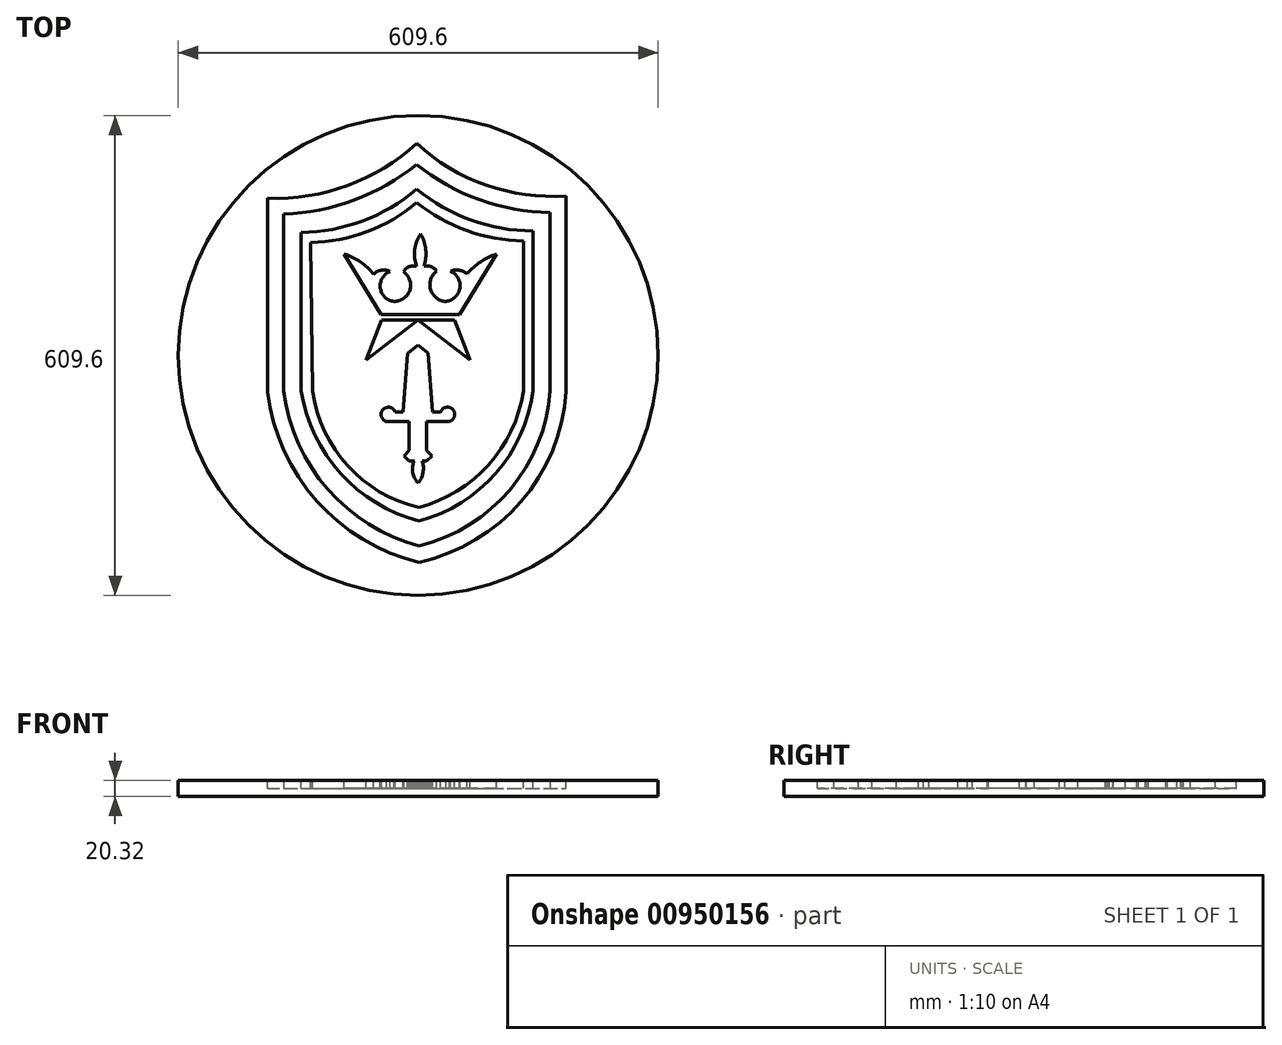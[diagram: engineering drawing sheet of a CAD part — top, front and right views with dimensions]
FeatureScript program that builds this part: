
annotation { "Feature Type Name" : "Feature", "Feature Type Description" : "" }
export const myFeature = defineFeature(function(context is Context, id is Id, definition is map)
    precondition{}
    {
        {
            var Q0;
            Q0=qCreatedBy(makeId("Top.planeOp"),FACE);
            var sketch = newSketch(context, id + "F0", { "sketchPlane" : qUnion([Q0])});
            skPoint(sketch, "E0.0", {"position": v(-45.7, 36.46) * mm});
            skPoint(sketch, "E1.0", {"position": v(53.8, 36.46) * mm});
            skPoint(sketch, "E2.0", {"position": v(100.8, 113.13) * mm});
            skPoint(sketch, "E3.0", {"position": v(63.63, 88.13) * mm});
            skPoint(sketch, "E4.0", {"position": v(42.63, 91.3) * mm});
            skPoint(sketch, "E5.0", {"position": v(25.13, 91.46) * mm});
            skPoint(sketch, "E6.0", {"position": v(8.8, 97.63) * mm});
            skPoint(sketch, "E7.0", {"position": v(-0.37, 97.46) * mm});
            skPoint(sketch, "E8.0", {"position": v(-17.03, 90.63) * mm});
            skPoint(sketch, "E9.0", {"position": v(-34.03, 91.13) * mm});
            skPoint(sketch, "E10.0", {"position": v(-55.2, 87.63) * mm});
            skPoint(sketch, "E11.0", {"position": v(-92.37, 113.13) * mm});
            skPoint(sketch, "E12.0", {"position": v(-64.53, -21.7) * mm});
            skPoint(sketch, "E13.0", {"position": v(-44.87, 29.46) * mm});
            skPoint(sketch, "E14.0", {"position": v(1.47, 29.46) * mm});
            skPoint(sketch, "E15.0", {"position": v(67.47, -21.7) * mm});
            skPoint(sketch, "E16.0", {"position": v(47.8, 29.46) * mm});
            skPoint(sketch, "E17.0", {"position": v(1.25, -2.29) * mm});
            skPoint(sketch, "E18.0", {"position": v(-12.12, -13.12) * mm});
            skPoint(sketch, "E19.0", {"position": v(-17.53, -87.54) * mm});
            skPoint(sketch, "E20.0", {"position": v(-27.71, -87.46) * mm});
            skPoint(sketch, "E21.0", {"position": v(-38.85, -99.54) * mm});
            skPoint(sketch, "E22.0", {"position": v(-10, -99.54) * mm});
            skPoint(sketch, "E23.0", {"position": v(12.13, -99.54) * mm});
            skPoint(sketch, "E24.0", {"position": v(29.97, -87.48) * mm});
            skPoint(sketch, "E25.0", {"position": v(19.97, -87.54) * mm});
            skPoint(sketch, "E26.0", {"position": v(14.13, -12.7) * mm});
            skPoint(sketch, "E27.0", {"position": v(19.02, -143.57) * mm});
            skPoint(sketch, "E28.0", {"position": v(12.3, -136.2) * mm});
            skPoint(sketch, "E29.0", {"position": v(-10.23, -136.2) * mm});
            skPoint(sketch, "E30.0", {"position": v(-16.22, -143.37) * mm});
            skPoint(sketch, "E31.0", {"position": v(-10.2, -149.54) * mm});
            skPoint(sketch, "E32.0", {"position": v(-3.2, -149.54) * mm});
            skPoint(sketch, "E33.0", {"position": v(1.8, -177.7) * mm});
            skPoint(sketch, "E34.0", {"position": v(6.61, -149.6) * mm});
            skPoint(sketch, "E35.0", {"position": v(11.99, -149.48) * mm});
            skPoint(sketch, "E36.0", {"position": v(-135.23, 127.8) * mm});
            skPoint(sketch, "E37.0", {"position": v(-147.23, 140.49) * mm});
            skPoint(sketch, "E38.0", {"position": v(-169.23, 163.75) * mm});
            skPoint(sketch, "E39.0", {"position": v(-0.37, 195.5) * mm});
            skPoint(sketch, "E40.0", {"position": v(-0.34, 178.32) * mm});
            skPoint(sketch, "E41.0", {"position": v(135.23, 129.67) * mm});
            skPoint(sketch, "E42.0", {"position": v(169.23, 166.1) * mm});
            skPoint(sketch, "E43.0", {"position": v(-0.43, 226.98) * mm});
            skPoint(sketch, "E44.0", {"position": v(2.93, -257.46) * mm});
            skPoint(sketch, "E45.0", {"position": v(2.55, -225.97) * mm});
            skPoint(sketch, "E46.0", {"position": v(2.34, -208.8) * mm});
            skLineSegment(sketch, "E47", {"start": v(-64.53, -21.7) * mm, "end": v(1.47, 29.46) * mm});
            skLineSegment(sketch, "E48", {"start": v(-44.87, 29.46) * mm, "end": v(-64.53, -21.7) * mm});
            skLineSegment(sketch, "E49", {"start": v(-44.87, 29.46) * mm, "end": v(1.47, 29.46) * mm});
            skLineSegment(sketch, "E50", {"start": v(1.47, 29.46) * mm, "end": v(47.8, 29.46) * mm});
            skLineSegment(sketch, "E51", {"start": v(67.47, -21.7) * mm, "end": v(47.8, 29.46) * mm});
            skLineSegment(sketch, "E52", {"start": v(67.47, -21.7) * mm, "end": v(1.47, 29.46) * mm});
            skLineSegment(sketch, "E53", {"start": v(1.25, -2.29) * mm, "end": v(-12.12, -13.12) * mm});
            skLineSegment(sketch, "E54", {"start": v(1.25, -2.29) * mm, "end": v(14.13, -12.7) * mm});
            skLineSegment(sketch, "E55", {"start": v(-12.12, -13.12) * mm, "end": v(-17.53, -87.54) * mm});
            skLineSegment(sketch, "E56", {"start": v(-17.53, -87.54) * mm, "end": v(-27.71, -87.46) * mm});
            skLineSegment(sketch, "E57", {"start": v(19.97, -87.54) * mm, "end": v(29.97, -87.48) * mm});
            skPoint(sketch, "E58.0", {"position": v(41.07, -99.54) * mm});
            skLineSegment(sketch, "E59", {"start": v(-38.85, -99.54) * mm, "end": v(-10, -99.54) * mm});
            skLineSegment(sketch, "E60", {"start": v(12.13, -99.54) * mm, "end": v(41.07, -99.54) * mm});
            skLineSegment(sketch, "E61", {"start": v(-10.23, -136.2) * mm, "end": v(-10, -99.54) * mm});
            skLineSegment(sketch, "E62", {"start": v(12.13, -99.54) * mm, "end": v(12.3, -136.2) * mm});
            skLineSegment(sketch, "E63", {"start": v(-10.23, -136.2) * mm, "end": v(-16.22, -143.37) * mm});
            skLineSegment(sketch, "E64", {"start": v(-16.22, -143.37) * mm, "end": v(-10.2, -149.54) * mm});
            skLineSegment(sketch, "E65", {"start": v(-10.2, -149.54) * mm, "end": v(-3.2, -149.54) * mm});
            skLineSegment(sketch, "E66", {"start": v(6.61, -149.6) * mm, "end": v(11.99, -149.48) * mm});
            skLineSegment(sketch, "E67", {"start": v(11.99, -149.48) * mm, "end": v(19.02, -143.57) * mm});
            skLineSegment(sketch, "E68", {"start": v(19.02, -143.57) * mm, "end": v(12.3, -136.2) * mm});
            skArc(sketch, "E69", {"start": v(-34.03, 91.13) * mm, "mid": v(-45.15, 92.6) * mm, "end": v(-55.2, 87.63) * mm});
            skArc(sketch, "E70", {"start": v(-55.2, 87.63) * mm, "mid": v(-71.81, 103.25) * mm, "end": v(-92.37, 113.13) * mm});
            skArc(sketch, "E71", {"start": v(-0.37, 97.46) * mm, "mid": v(-9.95, 97.09) * mm, "end": v(-17.03, 90.63) * mm});
            skArc(sketch, "E72", {"start": v(25.13, 91.46) * mm, "mid": v(17.9, 97) * mm, "end": v(8.8, 97.63) * mm});
            skPoint(sketch, "E73.0", {"position": v(4.8, 138.8) * mm});
            skArc(sketch, "E74", {"start": v(4.8, 138.8) * mm, "mid": v(-2.9, 118.77) * mm, "end": v(-0.37, 97.46) * mm});
            skArc(sketch, "E75", {"start": v(8.8, 97.63) * mm, "mid": v(11.16, 118.63) * mm, "end": v(4.8, 138.8) * mm});
            skArc(sketch, "E76", {"start": v(-34.03, 91.13) * mm, "mid": v(-46.67, 70.15) * mm, "end": v(-29.22, 52.98) * mm});
            skArc(sketch, "E77", {"start": v(-29.22, 52.98) * mm, "mid": v(-9.14, 67.28) * mm, "end": v(-17.03, 90.63) * mm});
            skArc(sketch, "E78", {"start": v(25.13, 91.46) * mm, "mid": v(17.18, 68.05) * mm, "end": v(36.78, 52.98) * mm});
            skArc(sketch, "E79", {"start": v(36.78, 52.98) * mm, "mid": v(54.45, 69.88) * mm, "end": v(42.63, 91.3) * mm});
            skArc(sketch, "E80", {"start": v(63.63, 88.13) * mm, "mid": v(53.57, 92.64) * mm, "end": v(42.63, 91.3) * mm});
            skArc(sketch, "E81", {"start": v(100.8, 113.13) * mm, "mid": v(80.58, 103.06) * mm, "end": v(63.63, 88.13) * mm});
            skLineSegment(sketch, "E82", {"start": v(53.8, 36.46) * mm, "end": v(100.8, 113.13) * mm});
            skLineSegment(sketch, "E83", {"start": v(-45.7, 36.46) * mm, "end": v(53.8, 36.46) * mm});
            skLineSegment(sketch, "E84", {"start": v(-45.7, 36.46) * mm, "end": v(-92.37, 113.13) * mm});
            skArc(sketch, "E85", {"start": v(-27.71, -87.46) * mm, "mid": v(-43.15, -84.4) * mm, "end": v(-38.85, -99.54) * mm});
            skArc(sketch, "E86", {"start": v(41.07, -99.54) * mm, "mid": v(45.52, -84.3) * mm, "end": v(29.97, -87.48) * mm});
            skArc(sketch, "E87", {"start": v(-3.2, -149.54) * mm, "mid": v(-5.54, -164.48) * mm, "end": v(1.8, -177.7) * mm});
            skArc(sketch, "E88", {"start": v(1.8, -177.7) * mm, "mid": v(7.65, -164.24) * mm, "end": v(6.61, -149.6) * mm});
            skPoint(sketch, "E89.0", {"position": v(135.23, -60.82) * mm});
            skLineSegment(sketch, "E90", {"start": v(135.23, -60.82) * mm, "end": v(-222.02, -60.82) * mm, "construction": true});
            skLineSegment(sketch, "E91", {"start": v(-222.02, -60.82) * mm, "end": v(135.23, -60.82) * mm, "construction": true});
            skLineSegment(sketch, "E92", {"start": v(218.08, -60.82) * mm, "end": v(135.23, -60.82) * mm, "construction": true});
            skLineSegment(sketch, "E93", {"start": v(-135.23, 127.8) * mm, "end": v(-132.62, -60.82) * mm});
            skLineSegment(sketch, "E94", {"start": v(-147.23, 140.49) * mm, "end": v(-147.23, -60.82) * mm});
            skLineSegment(sketch, "E95", {"start": v(135.23, 129.67) * mm, "end": v(135.23, -60.82) * mm});
            skPoint(sketch, "E96.0", {"position": v(147.23, 142.53) * mm});
            skLineSegment(sketch, "E97", {"start": v(147.23, 142.53) * mm, "end": v(147.23, -60.82) * mm});
            skArc(sketch, "E98", {"start": v(-147.23, -60.82) * mm, "mid": v(-96.87, -165.64) * mm, "end": v(2.55, -225.97) * mm});
            skArc(sketch, "E99", {"start": v(2.55, -225.97) * mm, "mid": v(100.07, -165.45) * mm, "end": v(147.23, -60.82) * mm});
            skArc(sketch, "E100", {"start": v(2.34, -208.8) * mm, "mid": v(90.9, -154.67) * mm, "end": v(135.23, -60.82) * mm});
            skArc(sketch, "E101", {"start": v(-132.62, -60.82) * mm, "mid": v(-88.12, -155.77) * mm, "end": v(2.34, -208.8) * mm});
            skArc(sketch, "E102", {"start": v(-0.34, 178.32) * mm, "mid": v(63.44, 142.85) * mm, "end": v(135.23, 129.67) * mm});
            skArc(sketch, "E103", {"start": v(-135.23, 127.8) * mm, "mid": v(-63.43, 141.43) * mm, "end": v(-0.34, 178.32) * mm});
            skArc(sketch, "E104", {"start": v(-147.23, 140.49) * mm, "mid": v(-69.02, 155.21) * mm, "end": v(-0.37, 195.5) * mm});
            skArc(sketch, "E105", {"start": v(-0.37, 195.5) * mm, "mid": v(68.84, 156.23) * mm, "end": v(147.23, 142.53) * mm});
            skArc(sketch, "E106", {"start": v(-0.43, 226.98) * mm, "mid": v(79.25, 182.2) * mm, "end": v(169.23, 166.1) * mm});
            skArc(sketch, "E107", {"start": v(-169.23, 163.75) * mm, "mid": v(-79.71, 181.7) * mm, "end": v(-0.43, 226.98) * mm});
            skLineSegment(sketch, "E108", {"start": v(-169.23, 163.75) * mm, "end": v(-169.23, -60.82) * mm});
            skLineSegment(sketch, "E109", {"start": v(169.23, 166.1) * mm, "end": v(169.23, -60.82) * mm});
            skArc(sketch, "E110", {"start": v(-169.23, -60.82) * mm, "mid": v(-113.37, -185.6) * mm, "end": v(2.93, -257.46) * mm});
            skArc(sketch, "E111", {"start": v(2.93, -257.46) * mm, "mid": v(118.16, -186.27) * mm, "end": v(169.23, -60.82) * mm});
            skSolve(sketch);
        }
        {
            var Q0;
            Q0=qCreatedBy(makeId("Top.planeOp"),FACE);
            var sketch = newSketch(context, id + "F1", { "sketchPlane" : qUnion([Q0])});
            skLineSegment(sketch, "E112.0", {"start": v(-169.23, 163.75) * mm, "end": v(-169.23, -60.82) * mm});
            skArc(sketch, "E113.0", {"start": v(-169.23, -60.82) * mm, "mid": v(-113.37, -185.6) * mm, "end": v(2.93, -257.46) * mm});
            skArc(sketch, "E114.0", {"start": v(2.93, -257.46) * mm, "mid": v(118.16, -186.27) * mm, "end": v(169.23, -60.82) * mm});
            skLineSegment(sketch, "E115.0", {"start": v(169.23, 166.1) * mm, "end": v(169.23, -60.82) * mm});
            skArc(sketch, "E116.0", {"start": v(-0.43, 226.98) * mm, "mid": v(79.25, 182.2) * mm, "end": v(169.23, 166.1) * mm});
            skArc(sketch, "E117.0", {"start": v(-169.23, 163.75) * mm, "mid": v(-79.71, 181.7) * mm, "end": v(-0.43, 226.98) * mm});
            skSolve(sketch);
        }
        {
            var Q0;
            Q0 = qSketchRegion(id + "F1", true);
            extrude(context, id + "F2", {"entities" : qUnion([Q0]), "depth" : 31.75 * mm, "offsetDistance" : 25.4 * mm});
        }
        {
            var Q0;
            Q0=makeQuery(id+"F2.opExtrude","CAP_FACE",FACE,{"disambiguationData":[OSD([sQuery(id+"F1.wireOp",EDGE,"E112.0"),sQuery(id+"F1.wireOp",EDGE,"E113.0"),sQuery(id+"F1.wireOp",EDGE,"E114.0"),sQuery(id+"F1.wireOp",EDGE,"E115.0"),sQuery(id+"F1.wireOp",EDGE,"E116.0"),sQuery(id+"F1.wireOp",EDGE,"E117.0")])],"isStart":false});
            var sketch = newSketch(context, id + "F3", { "sketchPlane" : qUnion([Q0])});
            skLineSegment(sketch, "E118.0", {"start": v(-135.23, 127.8) * mm, "end": v(-132.62, -60.82) * mm});
            skLineSegment(sketch, "E119.0", {"start": v(-147.23, 140.49) * mm, "end": v(-147.23, -60.82) * mm});
            skArc(sketch, "E120.0", {"start": v(-135.23, 127.8) * mm, "mid": v(-63.43, 141.43) * mm, "end": v(-0.34, 178.32) * mm});
            skArc(sketch, "E121.0", {"start": v(-147.23, 140.49) * mm, "mid": v(-69.02, 155.21) * mm, "end": v(-0.37, 195.5) * mm});
            skArc(sketch, "E122.0", {"start": v(-0.34, 178.32) * mm, "mid": v(63.44, 142.85) * mm, "end": v(135.23, 129.67) * mm});
            skArc(sketch, "E123.0", {"start": v(-132.62, -60.82) * mm, "mid": v(-88.12, -155.77) * mm, "end": v(2.34, -208.8) * mm});
            skArc(sketch, "E124.0", {"start": v(-147.23, -60.82) * mm, "mid": v(-96.87, -165.64) * mm, "end": v(2.55, -225.97) * mm});
            skArc(sketch, "E125.0", {"start": v(2.34, -208.8) * mm, "mid": v(90.9, -154.67) * mm, "end": v(135.23, -60.82) * mm});
            skArc(sketch, "E126.0", {"start": v(2.55, -225.97) * mm, "mid": v(100.07, -165.45) * mm, "end": v(147.23, -60.82) * mm});
            skLineSegment(sketch, "E127.0", {"start": v(147.23, 142.53) * mm, "end": v(147.23, -60.82) * mm});
            skLineSegment(sketch, "E128.0", {"start": v(135.23, 129.67) * mm, "end": v(135.23, -60.82) * mm});
            skArc(sketch, "E129.0", {"start": v(-0.37, 195.5) * mm, "mid": v(68.84, 156.23) * mm, "end": v(147.23, 142.53) * mm});
            skSolve(sketch);
        }
        {
            var Q0;
            Q0 = qSketchRegion(id + "F3", true);
            extrude(context, id + "F4", {"entities" : qUnion([Q0]), "operationType" : NewBodyOperationType.REMOVE, "oppositeDirection" : true, "depth" : 11.43 * mm, "offsetDistance" : 25.4 * mm});
        }
        {
            var Q0;
            Q0=makeQuery(id+"F4.boolean.opBoolean","SPLIT",FACE,{"disambiguationData":[TD([makeQuery(id+"F4.opExtrude","SWEPT_FACE",FACE,{"disambiguationData":[OSD([sQuery(id+"F3.wireOp",EDGE,"E118.0")])]})])],"derivedFrom":makeQuery(id+"F2.opExtrude","CAP_FACE",FACE,{"disambiguationData":[OSD([sQuery(id+"F1.wireOp",EDGE,"E112.0"),sQuery(id+"F1.wireOp",EDGE,"E113.0"),sQuery(id+"F1.wireOp",EDGE,"E114.0"),sQuery(id+"F1.wireOp",EDGE,"E115.0"),sQuery(id+"F1.wireOp",EDGE,"E116.0"),sQuery(id+"F1.wireOp",EDGE,"E117.0")])],"isStart":false})});
            var sketch = newSketch(context, id + "F5", { "sketchPlane" : qUnion([Q0])});
            skLineSegment(sketch, "E130.0", {"start": v(-45.7, 36.46) * mm, "end": v(-92.37, 113.13) * mm});
            skArc(sketch, "E131.0", {"start": v(-55.2, 87.63) * mm, "mid": v(-71.81, 103.25) * mm, "end": v(-92.37, 113.13) * mm});
            skArc(sketch, "E132.0", {"start": v(-34.03, 91.13) * mm, "mid": v(-45.15, 92.6) * mm, "end": v(-55.2, 87.63) * mm});
            skArc(sketch, "E133.0", {"start": v(-34.03, 91.13) * mm, "mid": v(-46.67, 70.15) * mm, "end": v(-29.22, 52.98) * mm});
            skArc(sketch, "E134.0", {"start": v(-29.22, 52.98) * mm, "mid": v(-9.14, 67.28) * mm, "end": v(-17.03, 90.63) * mm});
            skPoint(sketch, "E135.0", {"position": v(-17.03, 90.63) * mm});
            skArc(sketch, "E136.0", {"start": v(-0.37, 97.46) * mm, "mid": v(-9.95, 97.09) * mm, "end": v(-17.03, 90.63) * mm});
            skArc(sketch, "E137.0", {"start": v(4.8, 138.8) * mm, "mid": v(-2.9, 118.77) * mm, "end": v(-0.37, 97.46) * mm});
            skArc(sketch, "E138.0", {"start": v(8.8, 97.63) * mm, "mid": v(11.16, 118.63) * mm, "end": v(4.8, 138.8) * mm});
            skArc(sketch, "E139.0", {"start": v(25.13, 91.46) * mm, "mid": v(17.9, 97) * mm, "end": v(8.8, 97.63) * mm});
            skArc(sketch, "E140.0", {"start": v(25.13, 91.46) * mm, "mid": v(17.18, 68.05) * mm, "end": v(36.78, 52.98) * mm});
            skArc(sketch, "E141.0", {"start": v(36.78, 52.98) * mm, "mid": v(54.45, 69.88) * mm, "end": v(42.63, 91.3) * mm});
            skArc(sketch, "E142.0", {"start": v(63.63, 88.13) * mm, "mid": v(53.57, 92.64) * mm, "end": v(42.63, 91.3) * mm});
            skArc(sketch, "E143.0", {"start": v(100.8, 113.13) * mm, "mid": v(80.58, 103.06) * mm, "end": v(63.63, 88.13) * mm});
            skPoint(sketch, "E144.0", {"position": v(77.3, 74.8) * mm});
            skLineSegment(sketch, "E145.0", {"start": v(53.8, 36.46) * mm, "end": v(100.8, 113.13) * mm});
            skLineSegment(sketch, "E146.0", {"start": v(-45.7, 36.46) * mm, "end": v(53.8, 36.46) * mm});
            skLineSegment(sketch, "E147.0", {"start": v(1.47, 29.46) * mm, "end": v(47.8, 29.46) * mm});
            skLineSegment(sketch, "E148.0", {"start": v(67.47, -21.7) * mm, "end": v(1.47, 29.46) * mm});
            skLineSegment(sketch, "E149.0", {"start": v(67.47, -21.7) * mm, "end": v(47.8, 29.46) * mm});
            skLineSegment(sketch, "E150.0", {"start": v(-64.53, -21.7) * mm, "end": v(1.47, 29.46) * mm});
            skPoint(sketch, "E151.0", {"position": v(-21.7, 29.46) * mm});
            skLineSegment(sketch, "E152.0", {"start": v(-44.87, 29.46) * mm, "end": v(1.47, 29.46) * mm});
            skLineSegment(sketch, "E153.0", {"start": v(-44.87, 29.46) * mm, "end": v(-64.53, -21.7) * mm});
            skLineSegment(sketch, "E154.0", {"start": v(-12.12, -13.12) * mm, "end": v(-17.53, -87.54) * mm});
            skLineSegment(sketch, "E155.0", {"start": v(1.25, -2.29) * mm, "end": v(-12.12, -13.12) * mm});
            skPoint(sketch, "E156.0", {"position": v(14.13, -12.7) * mm});
            skPoint(sketch, "E157.0", {"position": v(7.69, -7.5) * mm});
            skPoint(sketch, "E158.0", {"position": v(-22.62, -87.5) * mm});
            skLineSegment(sketch, "E159.0", {"start": v(-17.53, -87.54) * mm, "end": v(-27.71, -87.46) * mm});
            skArc(sketch, "E160.0", {"start": v(-27.71, -87.46) * mm, "mid": v(-43.15, -84.4) * mm, "end": v(-38.85, -99.54) * mm});
            skLineSegment(sketch, "E161.0", {"start": v(-38.85, -99.54) * mm, "end": v(-10, -99.54) * mm});
            skLineSegment(sketch, "E162.0", {"start": v(-10.23, -136.2) * mm, "end": v(-10, -99.54) * mm});
            skLineSegment(sketch, "E163.0", {"start": v(12.13, -99.54) * mm, "end": v(41.07, -99.54) * mm});
            skLineSegment(sketch, "E164.0", {"start": v(19.97, -87.54) * mm, "end": v(29.97, -87.48) * mm});
            skArc(sketch, "E165.0", {"start": v(41.07, -99.54) * mm, "mid": v(45.52, -84.3) * mm, "end": v(29.97, -87.48) * mm});
            skLineSegment(sketch, "E166.0", {"start": v(12.13, -99.54) * mm, "end": v(12.3, -136.2) * mm});
            skLineSegment(sketch, "E167.0", {"start": v(19.02, -143.57) * mm, "end": v(12.3, -136.2) * mm});
            skLineSegment(sketch, "E168.0", {"start": v(-10.23, -136.2) * mm, "end": v(-16.22, -143.37) * mm});
            skLineSegment(sketch, "E169.0", {"start": v(-16.22, -143.37) * mm, "end": v(-10.2, -149.54) * mm});
            skPoint(sketch, "E170.0", {"position": v(-6.7, -149.54) * mm});
            skLineSegment(sketch, "E171.0", {"start": v(-10.2, -149.54) * mm, "end": v(-3.2, -149.54) * mm});
            skArc(sketch, "E172.0", {"start": v(-3.2, -149.54) * mm, "mid": v(-5.54, -164.48) * mm, "end": v(1.8, -177.7) * mm});
            skArc(sketch, "E173.0", {"start": v(1.8, -177.7) * mm, "mid": v(7.65, -164.24) * mm, "end": v(6.61, -149.6) * mm});
            skLineSegment(sketch, "E174.0", {"start": v(6.61, -149.6) * mm, "end": v(11.99, -149.48) * mm});
            skLineSegment(sketch, "E175.0", {"start": v(11.99, -149.48) * mm, "end": v(19.02, -143.57) * mm});
            skLineSegment(sketch, "E176.0", {"start": v(1.25, -2.29) * mm, "end": v(14.13, -12.7) * mm});
            skLineSegment(sketch, "E177", {"start": v(14.13, -12.7) * mm, "end": v(19.97, -87.54) * mm});
            skSolve(sketch);
        }
        {
            var Q0;
            Q0=makeQuery(id+"F5.imprint","IMPRINT",FACE,{"disambiguationData":[TD([[makeQuery(id+"F5.imprint","IMPRINT",EDGE,{"derivedFrom":sQuery(id+"F5.wireOp",EDGE,"E130.0")}),-1.0]])]});
            extrude(context, id + "F6", {"entities" : qUnion([Q0]), "operationType" : NewBodyOperationType.REMOVE, "oppositeDirection" : true, "depth" : 8.9 * mm, "offsetDistance" : 25.4 * mm});
        }
        {
            var Q0;
            Q0=makeQuery(id+"F4.boolean.opBoolean","SPLIT",FACE,{"disambiguationData":[TD([makeQuery(id+"F4.opExtrude","SWEPT_FACE",FACE,{"disambiguationData":[OSD([sQuery(id+"F3.wireOp",EDGE,"E118.0")])]})])],"derivedFrom":makeQuery(id+"F2.opExtrude","CAP_FACE",FACE,{"disambiguationData":[OSD([sQuery(id+"F1.wireOp",EDGE,"E112.0"),sQuery(id+"F1.wireOp",EDGE,"E113.0"),sQuery(id+"F1.wireOp",EDGE,"E114.0"),sQuery(id+"F1.wireOp",EDGE,"E115.0"),sQuery(id+"F1.wireOp",EDGE,"E116.0"),sQuery(id+"F1.wireOp",EDGE,"E117.0")])],"isStart":false})});
            var sketch = newSketch(context, id + "F7", { "sketchPlane" : qUnion([Q0])});
            skLineSegment(sketch, "E178.0", {"start": v(67.47, -21.7) * mm, "end": v(47.8, 29.46) * mm});
            skLineSegment(sketch, "E179", {"start": v(47.8, 29.46) * mm, "end": v(1.88, 29.46) * mm});
            skLineSegment(sketch, "E180", {"start": v(1.88, 29.46) * mm, "end": v(67.47, -21.7) * mm});
            skSolve(sketch);
        }
        {
            var Q0;
            Q0 = qSketchRegion(id + "F7", true);
            extrude(context, id + "F8", {"entities" : qUnion([Q0]), "operationType" : NewBodyOperationType.REMOVE, "oppositeDirection" : true, "depth" : 8.9 * mm, "offsetDistance" : 25.4 * mm});
        }
        {
            var Q0;
            Q0=makeQuery(id+"F4.boolean.opBoolean","SPLIT",FACE,{"disambiguationData":[TD([makeQuery(id+"F4.opExtrude","SWEPT_FACE",FACE,{"disambiguationData":[OSD([sQuery(id+"F3.wireOp",EDGE,"E118.0")])]})])],"derivedFrom":makeQuery(id+"F2.opExtrude","CAP_FACE",FACE,{"disambiguationData":[OSD([sQuery(id+"F1.wireOp",EDGE,"E112.0"),sQuery(id+"F1.wireOp",EDGE,"E113.0"),sQuery(id+"F1.wireOp",EDGE,"E114.0"),sQuery(id+"F1.wireOp",EDGE,"E115.0"),sQuery(id+"F1.wireOp",EDGE,"E116.0"),sQuery(id+"F1.wireOp",EDGE,"E117.0")])],"isStart":false})});
            var sketch = newSketch(context, id + "F9", { "sketchPlane" : qUnion([Q0])});
            skLineSegment(sketch, "E181.0", {"start": v(-44.87, 29.46) * mm, "end": v(-64.53, -21.7) * mm});
            skLineSegment(sketch, "E182.0", {"start": v(-44.87, 29.46) * mm, "end": v(1.05, 29.46) * mm});
            skLineSegment(sketch, "E183", {"start": v(1.05, 29.46) * mm, "end": v(-64.53, -21.7) * mm});
            skPoint(sketch, "E184.orphan", {"position": v(1.47, 29.46) * mm});
            skSolve(sketch);
        }
        {
            var Q0;
            Q0 = qSketchRegion(id + "F9", true);
            extrude(context, id + "F10", {"entities" : qUnion([Q0]), "operationType" : NewBodyOperationType.REMOVE, "oppositeDirection" : true, "depth" : 8.9 * mm, "offsetDistance" : 25.4 * mm});
        }
        {
            var Q0;
            Q0=makeQuery(id+"F4.boolean.opBoolean","SPLIT",FACE,{"disambiguationData":[TD([makeQuery(id+"F4.opExtrude","SWEPT_FACE",FACE,{"disambiguationData":[OSD([sQuery(id+"F3.wireOp",EDGE,"E118.0")])]})])],"derivedFrom":makeQuery(id+"F2.opExtrude","CAP_FACE",FACE,{"disambiguationData":[OSD([sQuery(id+"F1.wireOp",EDGE,"E112.0"),sQuery(id+"F1.wireOp",EDGE,"E113.0"),sQuery(id+"F1.wireOp",EDGE,"E114.0"),sQuery(id+"F1.wireOp",EDGE,"E115.0"),sQuery(id+"F1.wireOp",EDGE,"E116.0"),sQuery(id+"F1.wireOp",EDGE,"E117.0")])],"isStart":false})});
            var sketch = newSketch(context, id + "F11", { "sketchPlane" : qUnion([Q0])});
            skLineSegment(sketch, "E185.0", {"start": v(-12.12, -13.12) * mm, "end": v(-17.53, -87.54) * mm});
            skLineSegment(sketch, "E186.0", {"start": v(1.25, -2.29) * mm, "end": v(-12.12, -13.12) * mm});
            skLineSegment(sketch, "E187.0", {"start": v(1.25, -2.29) * mm, "end": v(14.13, -12.7) * mm});
            skLineSegment(sketch, "E188.0", {"start": v(-17.53, -87.54) * mm, "end": v(-27.71, -87.46) * mm});
            skArc(sketch, "E189.0", {"start": v(-27.71, -87.46) * mm, "mid": v(-43.15, -84.4) * mm, "end": v(-38.85, -99.54) * mm});
            skLineSegment(sketch, "E190.0", {"start": v(-38.85, -99.54) * mm, "end": v(-10, -99.54) * mm});
            skLineSegment(sketch, "E191.0", {"start": v(-10.23, -136.2) * mm, "end": v(-10, -99.54) * mm});
            skLineSegment(sketch, "E192.0", {"start": v(12.13, -99.54) * mm, "end": v(12.3, -136.2) * mm});
            skLineSegment(sketch, "E193.0", {"start": v(12.13, -99.54) * mm, "end": v(41.07, -99.54) * mm});
            skLineSegment(sketch, "E194.0", {"start": v(19.97, -87.54) * mm, "end": v(29.97, -87.48) * mm});
            skArc(sketch, "E195.0", {"start": v(41.07, -99.54) * mm, "mid": v(45.52, -84.3) * mm, "end": v(29.97, -87.48) * mm});
            skLineSegment(sketch, "E196.0", {"start": v(19.02, -143.57) * mm, "end": v(12.3, -136.2) * mm});
            skLineSegment(sketch, "E197.0", {"start": v(-10.23, -136.2) * mm, "end": v(-16.22, -143.37) * mm});
            skLineSegment(sketch, "E198.0", {"start": v(-16.22, -143.37) * mm, "end": v(-10.2, -149.54) * mm});
            skLineSegment(sketch, "E199.0", {"start": v(-10.2, -149.54) * mm, "end": v(-3.2, -149.54) * mm});
            skArc(sketch, "E200.0", {"start": v(-3.2, -149.54) * mm, "mid": v(-5.54, -164.48) * mm, "end": v(1.8, -177.7) * mm});
            skArc(sketch, "E201.0", {"start": v(1.8, -177.7) * mm, "mid": v(7.65, -164.24) * mm, "end": v(6.61, -149.6) * mm});
            skLineSegment(sketch, "E202.0", {"start": v(6.61, -149.6) * mm, "end": v(11.99, -149.48) * mm});
            skLineSegment(sketch, "E203.0", {"start": v(11.99, -149.48) * mm, "end": v(19.02, -143.57) * mm});
            skLineSegment(sketch, "E204", {"start": v(14.13, -12.7) * mm, "end": v(19.97, -87.54) * mm});
            skSolve(sketch);
        }
        {
            var Q0;
            Q0 = qSketchRegion(id + "F11", true);
            extrude(context, id + "F12", {"entities" : qUnion([Q0]), "operationType" : NewBodyOperationType.REMOVE, "oppositeDirection" : true, "depth" : 8.9 * mm, "offsetDistance" : 25.4 * mm});
        }
        {
            var Q0;
            Q0=makeQuery(id+"F0.imprint","IMPRINT",FACE,{"disambiguationData":[TD([[makeQuery(id+"F0.imprint","IMPRINT",EDGE,{"derivedFrom":sQuery(id+"F0.wireOp",EDGE,"E94")}),-1.0]])]});
            var sketch = newSketch(context, id + "F13", { "sketchPlane" : qUnion([Q0])});
            skLineSegment(sketch, "E205", {"start": v(0, 228.06) * mm, "end": v(2.97, -257.25) * mm, "construction": true});
            skLineSegment(sketch, "E206", {"start": v(-282.53, -15.67) * mm, "end": v(226.71, -15.67) * mm, "construction": true});
            skLineSegment(sketch, "E207", {"start": v(2.97, -257.25) * mm, "end": v(237.48, -255.81) * mm, "construction": true});
            skLineSegment(sketch, "E208", {"start": v(0, 228.06) * mm, "end": v(361.96, 230.27) * mm, "construction": true});
            skCircle(sketch, "E209", {"center": v(1.5, -15.67) * mm, "radius": 304.8 * mm});
            skSolve(sketch);
        }
        {
            var Q0;
            Q0 = qSketchRegion(id + "F13", true);
            extrude(context, id + "F14", {"entities" : qUnion([Q0]), "operationType" : NewBodyOperationType.ADD, "oppositeDirection" : true, "depth" : 20.32 * mm, "offsetDistance" : 25.4 * mm});
        }
        {
            var Q0;
            Q0=makeQuery(id+"F14.opExtrude","CAP_FACE",FACE,{"disambiguationData":[OSD([sQuery(id+"F13.wireOp",EDGE,"E209")])],"isStart":true});
            var sketch = newSketch(context, id + "F15", { "sketchPlane" : qUnion([Q0])});
            skLineSegment(sketch, "E210.0", {"start": v(-169.23, 163.75) * mm, "end": v(-169.23, -60.82) * mm});
            skArc(sketch, "E211.0", {"start": v(-169.23, 163.75) * mm, "mid": v(-79.71, 181.7) * mm, "end": v(-0.43, 226.98) * mm});
            skArc(sketch, "E212.0", {"start": v(-0.43, 226.98) * mm, "mid": v(79.25, 182.2) * mm, "end": v(169.23, 166.1) * mm});
            skLineSegment(sketch, "E213.0", {"start": v(169.23, 166.1) * mm, "end": v(169.23, -60.82) * mm});
            skArc(sketch, "E214.0", {"start": v(-169.23, -60.82) * mm, "mid": v(-113.37, -185.6) * mm, "end": v(2.93, -257.46) * mm});
            skArc(sketch, "E215.0", {"start": v(2.93, -257.46) * mm, "mid": v(118.16, -186.27) * mm, "end": v(169.23, -60.82) * mm});
            skArc(sketch, "E216.0", {"start": v(-189.55, -62.04) * mm, "mid": v(-127.4, -200.42) * mm, "end": v(2.75, -278.36) * mm});
            skLineSegment(sketch, "E217.0", {"start": v(-189.55, 184.05) * mm, "end": v(-189.55, -62.04) * mm});
            skArc(sketch, "E218.0", {"start": v(-189.55, 184.05) * mm, "mid": v(-88.1, 200.27) * mm, "end": v(-0.41, 253.8) * mm});
            skArc(sketch, "E219.0", {"start": v(-0.41, 253.8) * mm, "mid": v(87.66, 200.78) * mm, "end": v(189.55, 187.03) * mm});
            skLineSegment(sketch, "E220.0", {"start": v(189.55, 187.03) * mm, "end": v(189.55, -61.53) * mm});
            skArc(sketch, "E221.0", {"start": v(2.75, -278.36) * mm, "mid": v(132.26, -201.05) * mm, "end": v(189.55, -61.53) * mm});
            skSolve(sketch);
        }
        {
            var Q0;
            Q0 = qSketchRegion(id + "F15", true);
            extrude(context, id + "F16", {"entities" : qUnion([Q0]), "operationType" : NewBodyOperationType.REMOVE, "oppositeDirection" : true, "depth" : 10.16 * mm, "offsetDistance" : 25.4 * mm});
        }
        {
            var Q0;
            Q0=makeQuery(id+"F14.opExtrude","CAP_FACE",FACE,{"disambiguationData":[OSD([sQuery(id+"F13.wireOp",EDGE,"E209")])],"isStart":true});
            var sketch = newSketch(context, id + "F17", { "sketchPlane" : qUnion([Q0])});
            skArc(sketch, "E222.0", {"start": v(-147.23, 140.49) * mm, "mid": v(-69.02, 155.21) * mm, "end": v(-0.37, 195.5) * mm});
            skLineSegment(sketch, "E223.0", {"start": v(-147.23, 140.49) * mm, "end": v(-147.23, -60.82) * mm});
            skLineSegment(sketch, "E224.0", {"start": v(-135.23, 127.8) * mm, "end": v(-132.62, -60.82) * mm});
            skArc(sketch, "E225.0", {"start": v(-135.23, 127.8) * mm, "mid": v(-63.43, 141.43) * mm, "end": v(-0.34, 178.32) * mm});
            skArc(sketch, "E226.0", {"start": v(-0.34, 178.32) * mm, "mid": v(63.44, 142.85) * mm, "end": v(135.23, 129.67) * mm});
            skArc(sketch, "E227.0", {"start": v(-0.37, 195.5) * mm, "mid": v(68.84, 156.23) * mm, "end": v(147.23, 142.53) * mm});
            skLineSegment(sketch, "E228.0", {"start": v(147.23, 142.53) * mm, "end": v(147.23, -60.82) * mm});
            skLineSegment(sketch, "E229.0", {"start": v(135.23, 129.67) * mm, "end": v(135.23, -60.82) * mm});
            skArc(sketch, "E230.0", {"start": v(2.34, -208.8) * mm, "mid": v(90.9, -154.67) * mm, "end": v(135.23, -60.82) * mm});
            skArc(sketch, "E231.0", {"start": v(2.55, -225.97) * mm, "mid": v(100.07, -165.45) * mm, "end": v(147.23, -60.82) * mm});
            skArc(sketch, "E232.0", {"start": v(-132.62, -60.82) * mm, "mid": v(-88.12, -155.77) * mm, "end": v(2.34, -208.8) * mm});
            skArc(sketch, "E233.0", {"start": v(-147.23, -60.82) * mm, "mid": v(-96.87, -165.64) * mm, "end": v(2.55, -225.97) * mm});
            skSolve(sketch);
        }
        {
            var Q0;
            Q0 = qSketchRegion(id + "F17", true);
            extrude(context, id + "F18", {"entities" : qUnion([Q0]), "operationType" : NewBodyOperationType.REMOVE, "oppositeDirection" : true, "depth" : 10.16 * mm, "offsetDistance" : 25.4 * mm});
        }
        {
            var Q0;
            Q0=makeQuery(id+"F14.opExtrude","CAP_FACE",FACE,{"disambiguationData":[OSD([sQuery(id+"F13.wireOp",EDGE,"E209")])],"isStart":true});
            var sketch = newSketch(context, id + "F19", { "sketchPlane" : qUnion([Q0])});
            skLineSegment(sketch, "E234.0", {"start": v(14.13, -12.7) * mm, "end": v(19.97, -87.54) * mm});
            skLineSegment(sketch, "E235.0", {"start": v(1.25, -2.29) * mm, "end": v(14.13, -12.7) * mm});
            skLineSegment(sketch, "E236.0", {"start": v(1.25, -2.29) * mm, "end": v(-12.12, -13.12) * mm});
            skLineSegment(sketch, "E237.0", {"start": v(-12.12, -13.12) * mm, "end": v(-17.53, -87.54) * mm});
            skLineSegment(sketch, "E238.0", {"start": v(-17.53, -87.54) * mm, "end": v(-27.71, -87.46) * mm});
            skArc(sketch, "E239.0", {"start": v(-27.71, -87.46) * mm, "mid": v(-43.15, -84.4) * mm, "end": v(-38.85, -99.54) * mm});
            skLineSegment(sketch, "E240.0", {"start": v(-38.85, -99.54) * mm, "end": v(-10, -99.54) * mm});
            skLineSegment(sketch, "E241.0", {"start": v(-10.23, -136.2) * mm, "end": v(-10, -99.54) * mm});
            skLineSegment(sketch, "E242.0", {"start": v(-10.23, -136.2) * mm, "end": v(-16.22, -143.37) * mm});
            skLineSegment(sketch, "E243.0", {"start": v(-16.22, -143.37) * mm, "end": v(-10.2, -149.54) * mm});
            skLineSegment(sketch, "E244.0", {"start": v(-10.2, -149.54) * mm, "end": v(-3.2, -149.54) * mm});
            skArc(sketch, "E245.0", {"start": v(-3.2, -149.54) * mm, "mid": v(-5.54, -164.48) * mm, "end": v(1.8, -177.7) * mm});
            skArc(sketch, "E246.0", {"start": v(1.8, -177.7) * mm, "mid": v(7.65, -164.24) * mm, "end": v(6.61, -149.6) * mm});
            skLineSegment(sketch, "E247.0", {"start": v(6.61, -149.6) * mm, "end": v(11.99, -149.48) * mm});
            skLineSegment(sketch, "E248.0", {"start": v(11.99, -149.48) * mm, "end": v(19.02, -143.57) * mm});
            skLineSegment(sketch, "E249.0", {"start": v(19.02, -143.57) * mm, "end": v(12.3, -136.2) * mm});
            skLineSegment(sketch, "E250.0", {"start": v(12.13, -99.54) * mm, "end": v(12.3, -136.2) * mm});
            skLineSegment(sketch, "E251.0", {"start": v(12.13, -99.54) * mm, "end": v(41.07, -99.54) * mm});
            skArc(sketch, "E252.0", {"start": v(41.07, -99.54) * mm, "mid": v(45.52, -84.3) * mm, "end": v(29.97, -87.48) * mm});
            skLineSegment(sketch, "E253.0", {"start": v(19.97, -87.54) * mm, "end": v(29.97, -87.48) * mm});
            skSolve(sketch);
        }
        {
            var Q0;
            Q0 = qSketchRegion(id + "F19", true);
            extrude(context, id + "F20", {"entities" : qUnion([Q0]), "operationType" : NewBodyOperationType.REMOVE, "oppositeDirection" : true, "depth" : 10.16 * mm, "offsetDistance" : 25.4 * mm});
        }
        {
            var Q0;
            Q0=makeQuery(id+"F14.opExtrude","CAP_FACE",FACE,{"disambiguationData":[OSD([sQuery(id+"F13.wireOp",EDGE,"E209")])],"isStart":true});
            var sketch = newSketch(context, id + "F21", { "sketchPlane" : qUnion([Q0])});
            skLineSegment(sketch, "E254.0", {"start": v(-44.87, 29.46) * mm, "end": v(1.05, 29.46) * mm});
            skLineSegment(sketch, "E255.0", {"start": v(1.05, 29.46) * mm, "end": v(-64.53, -21.7) * mm});
            skLineSegment(sketch, "E256.0", {"start": v(-44.87, 29.46) * mm, "end": v(-64.53, -21.7) * mm});
            skSolve(sketch);
        }
        {
            var Q0;
            Q0 = qSketchRegion(id + "F21", true);
            extrude(context, id + "F22", {"entities" : qUnion([Q0]), "operationType" : NewBodyOperationType.REMOVE, "oppositeDirection" : true, "depth" : 10.16 * mm, "offsetDistance" : 25.4 * mm});
        }
        {
            var Q0;
            Q0=makeQuery(id+"F14.opExtrude","CAP_FACE",FACE,{"disambiguationData":[OSD([sQuery(id+"F13.wireOp",EDGE,"E209")])],"isStart":true});
            var sketch = newSketch(context, id + "F23", { "sketchPlane" : qUnion([Q0])});
            skLineSegment(sketch, "E257.0", {"start": v(1.47, 29.46) * mm, "end": v(47.8, 29.46) * mm});
            skLineSegment(sketch, "E258.0", {"start": v(67.47, -21.7) * mm, "end": v(1.47, 29.46) * mm});
            skLineSegment(sketch, "E259.0", {"start": v(67.47, -21.7) * mm, "end": v(47.8, 29.46) * mm});
            skSolve(sketch);
        }
        {
            var Q0;
            Q0 = qSketchRegion(id + "F23", true);
            extrude(context, id + "F24", {"entities" : qUnion([Q0]), "operationType" : NewBodyOperationType.REMOVE, "oppositeDirection" : true, "depth" : 10.16 * mm, "offsetDistance" : 25.4 * mm});
        }
        {
            var Q0;
            Q0=makeQuery(id+"F14.opExtrude","CAP_FACE",FACE,{"disambiguationData":[OSD([sQuery(id+"F13.wireOp",EDGE,"E209")])],"isStart":true});
            var sketch = newSketch(context, id + "F25", { "sketchPlane" : qUnion([Q0])});
            skArc(sketch, "E260.0", {"start": v(-55.2, 87.63) * mm, "mid": v(-71.81, 103.25) * mm, "end": v(-92.37, 113.13) * mm});
            skLineSegment(sketch, "E261.0", {"start": v(-45.7, 36.46) * mm, "end": v(-92.37, 113.13) * mm});
            skArc(sketch, "E262.0", {"start": v(-34.03, 91.13) * mm, "mid": v(-46.67, 70.15) * mm, "end": v(-29.22, 52.98) * mm});
            skArc(sketch, "E263.0", {"start": v(-34.03, 91.13) * mm, "mid": v(-45.15, 92.6) * mm, "end": v(-55.2, 87.63) * mm});
            skArc(sketch, "E264.0", {"start": v(-29.22, 52.98) * mm, "mid": v(-9.14, 67.28) * mm, "end": v(-17.03, 90.63) * mm});
            skArc(sketch, "E265.0", {"start": v(-0.37, 97.46) * mm, "mid": v(-9.95, 97.09) * mm, "end": v(-17.03, 90.63) * mm});
            skArc(sketch, "E266.0", {"start": v(4.8, 138.8) * mm, "mid": v(-2.9, 118.77) * mm, "end": v(-0.37, 97.46) * mm});
            skArc(sketch, "E267.0", {"start": v(8.8, 97.63) * mm, "mid": v(11.16, 118.63) * mm, "end": v(4.8, 138.8) * mm});
            skArc(sketch, "E268.0", {"start": v(25.13, 91.46) * mm, "mid": v(17.9, 97) * mm, "end": v(8.8, 97.63) * mm});
            skArc(sketch, "E269.0", {"start": v(25.13, 91.46) * mm, "mid": v(17.18, 68.05) * mm, "end": v(36.78, 52.98) * mm});
            skLineSegment(sketch, "E270.0", {"start": v(-45.7, 36.46) * mm, "end": v(53.8, 36.46) * mm});
            skArc(sketch, "E271.0", {"start": v(36.78, 52.98) * mm, "mid": v(54.45, 69.88) * mm, "end": v(42.63, 91.3) * mm});
            skArc(sketch, "E272.0", {"start": v(63.63, 88.13) * mm, "mid": v(53.57, 92.64) * mm, "end": v(42.63, 91.3) * mm});
            skArc(sketch, "E273.0", {"start": v(100.8, 113.13) * mm, "mid": v(80.58, 103.06) * mm, "end": v(63.63, 88.13) * mm});
            skLineSegment(sketch, "E274.0", {"start": v(53.8, 36.46) * mm, "end": v(100.8, 113.13) * mm});
            skSolve(sketch);
        }
        {
            var Q0;
            Q0 = qSketchRegion(id + "F25", true);
            extrude(context, id + "F26", {"entities" : qUnion([Q0]), "operationType" : NewBodyOperationType.REMOVE, "oppositeDirection" : true, "depth" : 10.16 * mm, "offsetDistance" : 25.4 * mm});
        }
        {
            var Q0;
            Q0=makeQuery(id+"F14.opExtrude","CAP_FACE",FACE,{"disambiguationData":[OSD([sQuery(id+"F13.wireOp",EDGE,"E209")])],"isStart":true});
            var sketch = newSketch(context, id + "F27", { "sketchPlane" : qUnion([Q0])});
            skCircle(sketch, "E275.0", {"center": v(1.5, -15.67) * mm, "radius": 304.8 * mm});
            skSolve(sketch);
        }
        {
            var Q0;
            Q0 = qSketchRegion(id + "F27", true);
            extrude(context, id + "F28", {"entities" : qUnion([Q0]), "operationType" : NewBodyOperationType.REMOVE, "depth" : 38.1 * mm, "offsetDistance" : 25.4 * mm});
        }
    });
